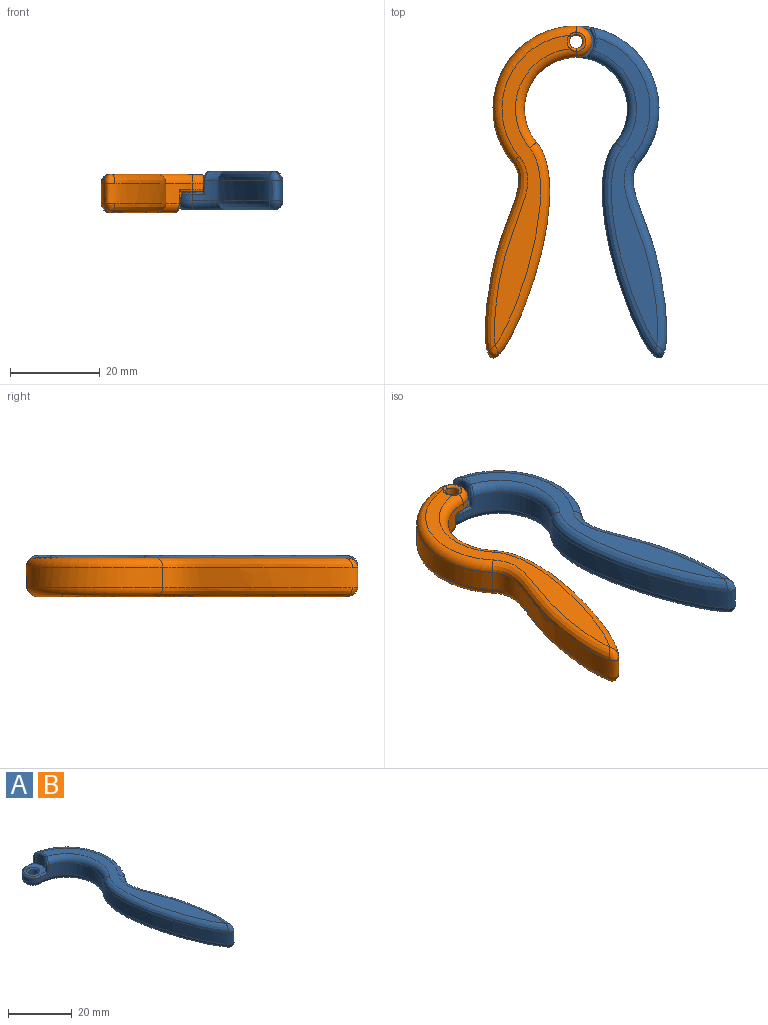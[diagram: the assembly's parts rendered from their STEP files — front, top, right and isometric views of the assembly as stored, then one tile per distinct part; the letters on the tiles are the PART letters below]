
ASSEMBLY  parts=2 mates=1
PART A: 33 faces, bbox 24x75.5x8.7 mm
  f0: cylinder r=4mm len=5.33mm, axis (0,0,-1), area 21.8mm2, adj f8,f20,f21,f23,f25,f27
  f1: cylinder r=11.5mm len=18.89mm, axis (0,0,-1), area 111.1mm2, adj f2,f7,f14,f19,f26,f27
  f2: extruded ~48.08x14.33mm, area 447mm2, adj f1,f3,f9,f10,f12,f16,f17,f18
  f3: cylinder r=18.5mm len=30.39mm, axis (0,0,-1), area 181.4mm2, adj f2,f7,f11,f15,f20,f22
  f4: plane 68.52x14.24mm, normal (0,0,1), area 266.2mm2, adj f15,f16,f18,f19,f23
  f5: plane 69.06x16.96mm, normal (0,0,-1), area 274.1mm2, adj f9,f11,f12,f14,f28
  f6: cylinder r=1.5mm len=3mm, axis (0,0,-1), area 27.8mm2, adj f28,f29,f30,f31,f32
  f7: cylinder r=3.5mm len=7mm, axis (0,0,-1), area 16.5mm2, adj f1,f3,f13,f24
  f8: plane 7x6.26mm, normal (0,0,1), area 23.1mm2, adj f0,f20,f22,f24,f26,f27,f32
  f9: bspline ~45.5x9.48mm, area 136.4mm2, adj f2,f5,f10,f11
  f10: bspline ~2.87x2.42mm, area 5.2mm2, adj f2,f9,f12
  f11: torus R=16.5mm, axis (0,0,1), area 126.2mm2, adj f3,f5,f9,f13,f29
  f12: bspline ~47.64x12.86mm, area 152.7mm2, adj f2,f5,f10,f14
  f13: torus R=1.5mm, axis (0,0,1), area 23.4mm2, adj f7,f11,f14,f31
  f14: torus R=13.5mm, axis (0,0,1), area 86.7mm2, adj f1,f5,f12,f13,f30
  f15: torus R=16.5mm, axis (0,0,1), area 113.5mm2, adj f3,f4,f16,f21
  f16: bspline ~50.71x9.48mm, area 136.4mm2, adj f2,f4,f15,f17
  f17: bspline ~2.87x2.42mm, area 5.2mm2, adj f2,f16,f18
  f18: bspline ~47.64x12.86mm, area 152.7mm2, adj f2,f4,f17,f19
  f19: torus R=13.5mm, axis (0,0,1), area 76.6mm2, adj f1,f4,f18,f25
  f20: cylinder r=0.5mm len=3.1mm, axis (0,0,1), area 3.3mm2, adj f0,f3,f8,f21,f22
  f21: bspline ~2.98x2.61mm, area 3.2mm2, adj f0,f15,f20,f23
  f22: torus R=18mm, axis (0,0,1), area 2.7mm2, adj f3,f8,f20,f24
  f23: torus R=4.5mm, axis (0,0,1), area 2.3mm2, adj f0,f4,f21,f25
  f24: torus R=3mm, axis (0,0,1), area 8.2mm2, adj f7,f8,f22,f26
  f25: bspline ~2.53x2.34mm, area 2.8mm2, adj f0,f19,f23,f27
  f26: torus R=12mm, axis (0,0,1), area 2.1mm2, adj f1,f8,f24,f27
  f27: cylinder r=0.5mm len=3.1mm, axis (0,0,-1), area 3mm2, adj f0,f1,f8,f25,f26
  f28: torus R=2mm, axis (0,0,1), area 2.2mm2, adj f5,f6,f29,f30
  f29: bspline ~2.12x1.32mm, area 1.2mm2, adj f6,f11,f28,f31
  f30: bspline ~2x1.21mm, area 1mm2, adj f6,f14,f28,f31
  f31: torus R=2mm, axis (0,0,-1), area 5.3mm2, adj f6,f13,f29,f30
  f32: torus R=2mm, axis (0,0,1), area 8.3mm2, adj f6,f8
PART B: same geometry as A
PLACE A rot(axis=(0,0,1),0deg) t=(-1.26,-1.21,4.25)mm
PLACE B rot(axis=(0,1,0),180deg) t=(-1.26,-1.21,12.25)mm
MATE revolute B.f0 <-> A.f0  axis (0,0,-1) through (-1.26,13.79,8.25)mm
